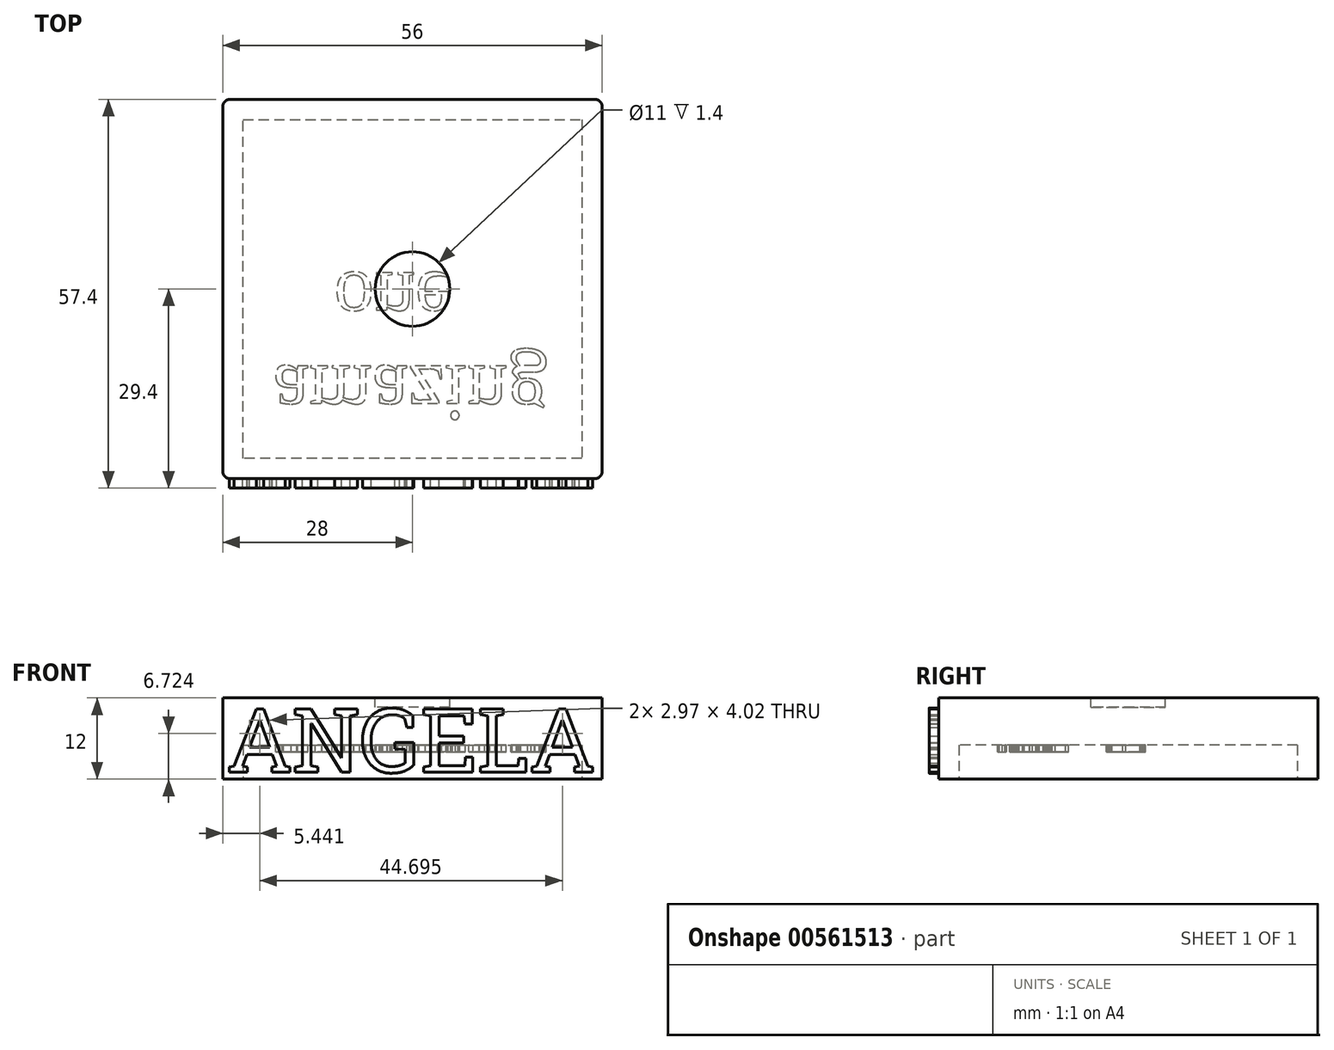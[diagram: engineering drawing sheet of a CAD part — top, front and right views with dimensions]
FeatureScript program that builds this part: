
annotation { "Feature Type Name" : "Feature", "Feature Type Description" : "" }
export const myFeature = defineFeature(function(context is Context, id is Id, definition is map)
    precondition{}
    {
        {
            var Q0;
            Q0=qCreatedBy(makeId("Top.planeOp"),FACE);
            var sketch = newSketch(context, id + "F0", { "sketchPlane" : qUnion([Q0])});
            skLineSegment(sketch, "E0.bottom", {"start": v(28, 28) * mm, "end": v(-28, 28) * mm});
            skLineSegment(sketch, "E0.top", {"start": v(28, -28) * mm, "end": v(-28, -28) * mm});
            skLineSegment(sketch, "E0.left", {"start": v(28, 28) * mm, "end": v(28, -28) * mm});
            skLineSegment(sketch, "E0.right", {"start": v(-28, 28) * mm, "end": v(-28, -28) * mm});
            skPoint(sketch, "E0.middle", {"position": v(0, 0) * mm});
            skSolve(sketch);
        }
        {
            var Q0;
            Q0=qSketchRegion(id+"F0",true);
            extrude(context, id + "F1", {"entities" : qUnion([Q0]), "depth" : 12 * mm, "offsetDistance" : 25 * mm});
        }
        {
            var Q0;
            Q0=makeQuery(id+"F1.opExtrude","SWEPT_FACE",FACE,{"disambiguationData":[OSD([sQuery(id+"F0.wireOp",EDGE,"E0.top")])]});
            var sketch = newSketch(context, id + "F2", { "sketchPlane" : qUnion([Q0])});
            skText(sketch, "E1", { "text": "ANGELA", "fontName": "RobotoSlab-Regular.ttf"});
            const initialGuessF2  = {"E1": [-0.0274, 0.001, 1, 0, 0.00948]};
            skSetInitialGuess(sketch, initialGuessF2);
            skSolve(sketch);
        }
        {
            var Q0;
            Q0=qSketchRegion(id+"F2",true);
            extrude(context, id + "F3", {"entities" : qUnion([Q0]), "depth" : 1.4 * mm, "offsetDistance" : 25 * mm});
        }
        {
            var Q0;
            Q0=makeQuery(id+"F1.opExtrude","SWEPT_EDGE",EDGE,{"disambiguationData":[OSD([sQuery(id+"F0.wireOp",EDGE,"E0.top"),sQuery(id+"F0.wireOp",EDGE,"E0.right")])]});
            var Q1;
            Q1=makeQuery(id+"F1.opExtrude","SWEPT_EDGE",EDGE,{"disambiguationData":[OSD([sQuery(id+"F0.wireOp",EDGE,"E0.bottom"),sQuery(id+"F0.wireOp",EDGE,"E0.right")])]});
            var Q2;
            Q2=makeQuery(id+"F1.opExtrude","SWEPT_EDGE",EDGE,{"disambiguationData":[OSD([sQuery(id+"F0.wireOp",EDGE,"E0.top"),sQuery(id+"F0.wireOp",EDGE,"E0.left")])]});
            var Q3;
            Q3=makeQuery(id+"F1.opExtrude","SWEPT_EDGE",EDGE,{"disambiguationData":[OSD([sQuery(id+"F0.wireOp",EDGE,"E0.bottom"),sQuery(id+"F0.wireOp",EDGE,"E0.left")])]});
            fillet(context, id + "F4", {"entities" : qUnion([Q0, Q1, Q2, Q3]), "radius" : 1 * mm, "tangentPropagation" : true, "allowEdgeOverflow" : false});
        }
        {
            var Q0;
            Q0=qCreatedBy(makeId("Front.planeOp"),FACE);
            var sketch = newSketch(context, id + "F5", { "sketchPlane" : qUnion([Q0])});
            skLineSegment(sketch, "E2", {"start": v(0, 0) * mm, "end": v(0, 77) * mm, "construction": true});
            skLineSegment(sketch, "E3", {"start": v(0, 77) * mm, "end": v(-25.6, 77) * mm});
            skLineSegment(sketch, "E4", {"start": v(0, 12) * mm, "end": v(-12, 12) * mm});
            skLineSegment(sketch, "E5", {"start": v(-25.6, 77) * mm, "end": v(-25.6, 68) * mm, "construction": true});
            skArc(sketch, "E6", {"start": v(-23.2, 60.2) * mm, "mid": v(-22.6, 62) * mm, "end": v(-23.2, 63.8) * mm});
            skLineSegment(sketch, "E7", {"start": v(-22.6, 77) * mm, "end": v(-22.6, 35) * mm, "construction": true});
            skArc(sketch, "E8", {"start": v(-25, 57.8) * mm, "mid": v(-25.6, 56) * mm, "end": v(-25, 54.2) * mm});
            skLineSegment(sketch, "E9", {"start": v(-25, 57.8) * mm, "end": v(-23.2, 60.2) * mm});
            skLineSegment(sketch, "E10", {"start": v(-25.6, 77) * mm, "end": v(-25.6, 68) * mm});
            skArc(sketch, "E11", {"start": v(-23.2, 48.2) * mm, "mid": v(-22.6, 50) * mm, "end": v(-23.2, 51.8) * mm});
            skLineSegment(sketch, "E12", {"start": v(-25, 54.2) * mm, "end": v(-23.2, 51.8) * mm});
            skArc(sketch, "E13", {"start": v(-25, 45.8) * mm, "mid": v(-25.6, 44) * mm, "end": v(-25, 42.2) * mm});
            skLineSegment(sketch, "E14", {"start": v(-23.2, 48.2) * mm, "end": v(-25, 45.8) * mm});
            skArc(sketch, "E15", {"start": v(-22.6, 38) * mm, "mid": v(-22.75, 38.95) * mm, "end": v(-23.2, 39.8) * mm});
            skLineSegment(sketch, "E16", {"start": v(-25, 42.2) * mm, "end": v(-23.2, 39.8) * mm});
            skArc(sketch, "E17", {"start": v(-25.6, 68) * mm, "mid": v(-25.45, 67.05) * mm, "end": v(-25, 66.2) * mm});
            skLineSegment(sketch, "E18", {"start": v(-25, 66.2) * mm, "end": v(-23.2, 63.8) * mm});
            skLineSegment(sketch, "E19.trimOffspring", {"start": v(-25.6, 65) * mm, "end": v(-25.6, 47) * mm, "construction": true});
            skLineSegment(sketch, "E20", {"start": v(-22.81, 39.11) * mm, "end": v(-13.2, 15) * mm});
            skLineSegment(sketch, "E21", {"start": v(0, 77) * mm, "end": v(0, 12) * mm});
            skArc(sketch, "E22", {"start": v(-15, 12) * mm, "mid": v(-13.62, 13.2) * mm, "end": v(-13.2, 15) * mm});
            skLineSegment(sketch, "E23", {"start": v(-15, 12) * mm, "end": v(-12, 12) * mm});
            skSolve(sketch);
        }
        {
            var Q0;
            Q0=qSketchRegion(id+"F5",true);
            var Q1;
            Q1=sQuery(id+"F5.wireOp",EDGE,"E21");
            revolve(context, id + "F6", {"entities" : qUnion([Q0]), "axis" : qUnion([Q1]), "revolveType" : RevolveType.FULL});
        }
        {
            var Q0;
            Q0=makeQuery(id+"F6.opRevolve","SWEPT_FACE",FACE,{"disambiguationData":[OSD([sQuery(id+"F5.wireOp",EDGE,"E3")])]});
            shell(context, id + "F7", {"entities" : qUnion([Q0]), "thickness" : 1.4 * mm});
        }
        {
            var Q0;
            Q0=makeQuery(id+"F6.opRevolve","SWEPT_EDGE",EDGE,{"disambiguationData":[OSD([sQuery(id+"F5.wireOp",EDGE,"E3"),sQuery(id+"F5.wireOp",EDGE,"E10")])]});
            fillet(context, id + "F8", {"entities" : qUnion([Q0]), "radius" : 2 * mm, "tangentPropagation" : true, "allowEdgeOverflow" : false});
        }
        {
            var Q0;
            Q0=makeQuery(id+"F7.opShell","OFFSET_FACE",FACE,{"disambiguationData":[OSD([sQuery(id+"F5.wireOp",EDGE,"E4")])]});
            var sketch = newSketch(context, id + "F9", { "sketchPlane" : qUnion([Q0])});
            skCircle(sketch, "E24", {"center": v(0, 0) * mm, "radius": 3.5 * mm});
            skCircle(sketch, "E25", {"center": v(0, 0) * mm, "radius": 4.5 * mm});
            skSolve(sketch);
        }
        {
            var Q0;
            Q0=qSketchRegion(id+"F9",true);
            extrude(context, id + "F10", {"entities" : qUnion([Q0]), "operationType" : NewBodyOperationType.ADD, "depth" : 5 * mm, "offsetDistance" : 25 * mm});
        }
        {
            var Q0;
            Q0=qCreatedBy(makeId("Front.planeOp"),FACE);
            var sketch = newSketch(context, id + "F11", { "sketchPlane" : qUnion([Q0])});
            skLineSegment(sketch, "E26.bottom", {"start": v(28, 77) * mm, "end": v(-28, 77) * mm});
            skLineSegment(sketch, "E26.top", {"start": v(28, 12) * mm, "end": v(-28, 12) * mm});
            skLineSegment(sketch, "E26.left", {"start": v(28, 77) * mm, "end": v(28, 12) * mm});
            skLineSegment(sketch, "E26.right", {"start": v(-28, 77) * mm, "end": v(-28, 12) * mm});
            skPoint(sketch, "E26.middle", {"position": v(0, 44.5) * mm});
            skSolve(sketch);
        }
        {
            var Q0;
            Q0 = qSketchRegion(id + "F11", true);
            extrude(context, id + "F12", {"entities" : qUnion([Q0]), "operationType" : NewBodyOperationType.REMOVE, "oppositeDirection" : true, "depth" : 30 * mm, "offsetDistance" : 25 * mm, "hasSecondDirection" : true, "secondDirectionOppositeDirection" : false, "secondDirectionDepth" : 30 * mm});
        }
        {
            var Q0;
            Q0=makeQuery(id+"F1.opExtrude","CAP_FACE",FACE,{"disambiguationData":[OSD([sQuery(id+"F0.wireOp",EDGE,"E0.bottom"),sQuery(id+"F0.wireOp",EDGE,"E0.top"),sQuery(id+"F0.wireOp",EDGE,"E0.left"),sQuery(id+"F0.wireOp",EDGE,"E0.right")])],"isStart":true});
            var sketch = newSketch(context, id + "F13", { "sketchPlane" : qUnion([Q0])});
            skLineSegment(sketch, "E27.0", {"start": v(25, -25) * mm, "end": v(25, 25) * mm});
            skLineSegment(sketch, "E27.1", {"start": v(-25, -25) * mm, "end": v(25, -25) * mm});
            skLineSegment(sketch, "E27.2", {"start": v(-25, 25) * mm, "end": v(-25, -25) * mm});
            skLineSegment(sketch, "E27.3", {"start": v(25, 25) * mm, "end": v(-25, 25) * mm});
            skSolve(sketch);
        }
        {
            var Q0;
            Q0 = qSketchRegion(id + "F13", true);
            extrude(context, id + "F14", {"entities" : qUnion([Q0]), "operationType" : NewBodyOperationType.REMOVE, "oppositeDirection" : true, "depth" : 5 * mm, "offsetDistance" : 25 * mm});
        }
        {
            var Q0;
            Q0=makeQuery(id+"F1.opExtrude","CAP_FACE",FACE,{"disambiguationData":[OSD([sQuery(id+"F0.wireOp",EDGE,"E0.bottom"),sQuery(id+"F0.wireOp",EDGE,"E0.top"),sQuery(id+"F0.wireOp",EDGE,"E0.left"),sQuery(id+"F0.wireOp",EDGE,"E0.right")])],"isStart":false});
            var sketch = newSketch(context, id + "F15", { "sketchPlane" : qUnion([Q0])});
            skCircle(sketch, "E28", {"center": v(0, 0) * mm, "radius": 5.5 * mm});
            skSolve(sketch);
        }
        {
            var Q0;
            Q0 = qSketchRegion(id + "F15", true);
            extrude(context, id + "F16", {"entities" : qUnion([Q0]), "operationType" : NewBodyOperationType.REMOVE, "oppositeDirection" : true, "depth" : 1.4 * mm, "offsetDistance" : 25 * mm});
        }
        {
            var Q0;
            Q0=makeQuery(id+"F14.boolean.opBoolean","COPY",FACE,{"derivedFrom":makeQuery(id+"F14.opExtrude","CAP_FACE",FACE,{"disambiguationData":[OSD([sQuery(id+"F13.wireOp",EDGE,"E27.0"),sQuery(id+"F13.wireOp",EDGE,"E27.1"),sQuery(id+"F13.wireOp",EDGE,"E27.2"),sQuery(id+"F13.wireOp",EDGE,"E27.3")])],"isStart":false})});
            var sketch = newSketch(context, id + "F17", { "sketchPlane" : qUnion([Q0])});
            skText(sketch, "E29", { "text": "amazing\n   one", "fontName": "Tinos-Regular.ttf"});
            const initialGuessF17  = {"E29": [-0.0206, 0.01137, 1, 0, 0.00863]};
            skSetInitialGuess(sketch, initialGuessF17);
            skSolve(sketch);
        }
        {
            var Q0;
            Q0 = qSketchRegion(id + "F17", true);
            extrude(context, id + "F18", {"entities" : qUnion([Q0]), "operationType" : NewBodyOperationType.ADD, "depth" : 1 * mm, "offsetDistance" : 25 * mm});
        }
    });
